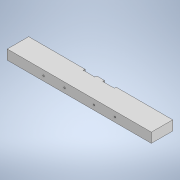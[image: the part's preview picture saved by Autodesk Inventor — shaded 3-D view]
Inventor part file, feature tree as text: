
AUTODESK INVENTOR PART (.ipt)
format: ipt  version: 2020 (Build 240168000, 168)  size: 173,056 bytes
history: native  units: mm
features: other x5, hole x3, sketch x3, projected_geometry x2, extrude x1
ambient origin geometry x8: Origin, YZ Plane, XZ Plane, XY Plane, X Axis, Y Axis, Z Axis, Center Point
bodies: Body1 (feature_tree)
feature tree (14):
  other  "작업 평면1"
  other  "작업 평면4"
  extrude  "돌출3"  Depth=25.0mm TaperAngle=0.0deg
  hole  "구멍1"  [1 undecoded]
  hole  "구멍2"  [1 undecoded]
  hole  "구멍3"  [1 undecoded]
  sketch  "스케치4"
  sketch  "스케치6"
  projected_geometry  "투영된 루프4"
  projected_geometry  "투영된 루프5"
  sketch  "스케치10"
  other  "<userpath>\Documents\Inventor\CoMoVi\Design4\v4.iam"
  other  "v4.iam"
  other  "AL_profile_final:1"
note: 3 required parameter values undecoded (feature->parameter linkage not recoverable at this tier; creation-order binding heuristic only, values carry confidence <= 0.55)
